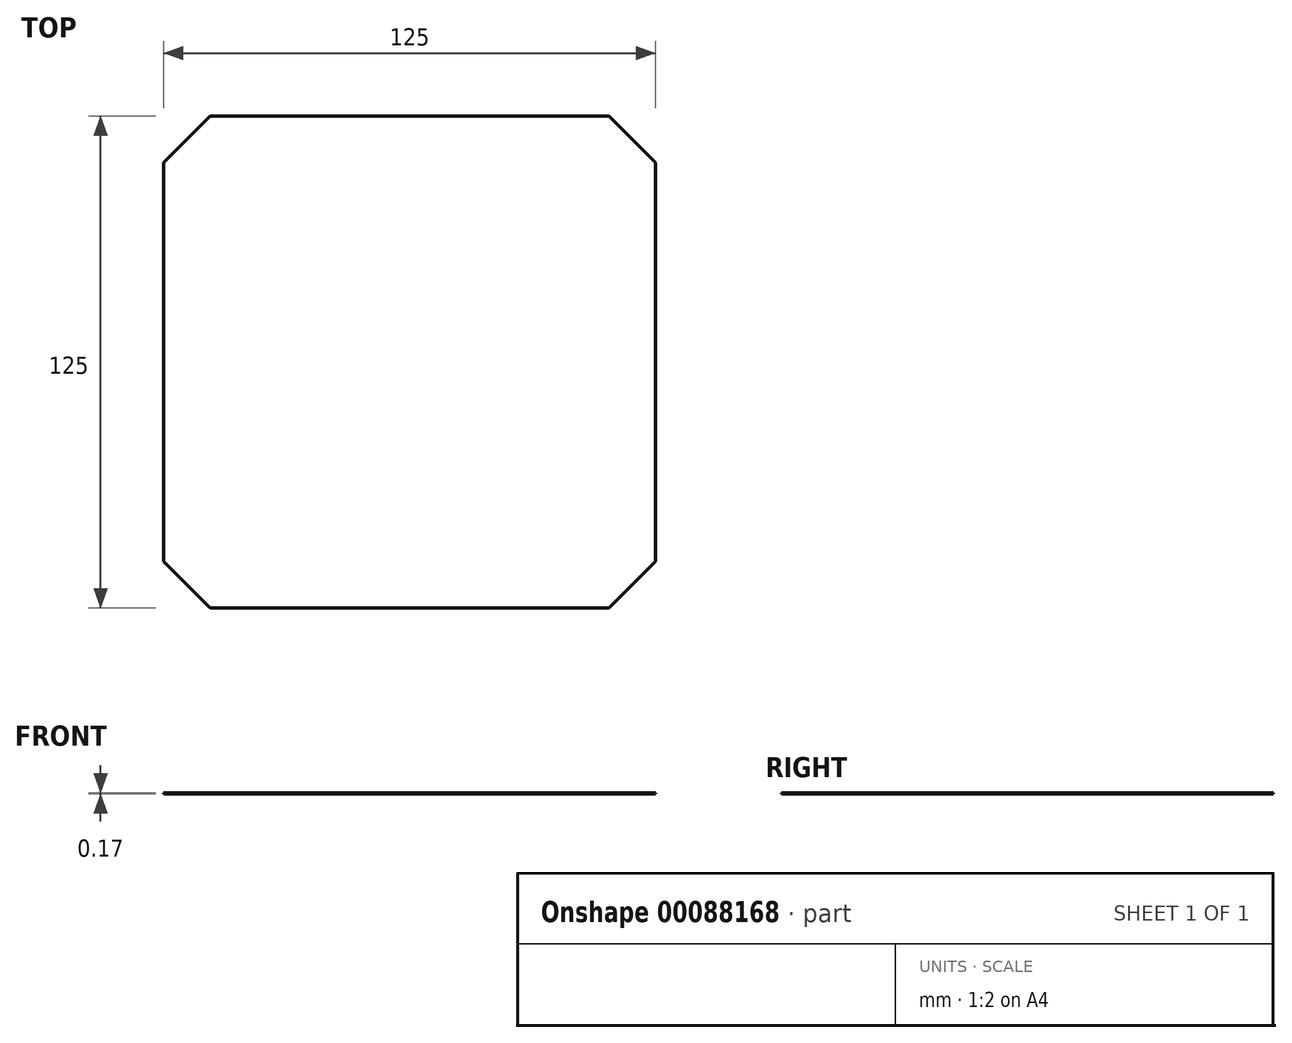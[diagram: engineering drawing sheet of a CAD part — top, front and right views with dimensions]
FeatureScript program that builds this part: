
annotation { "Feature Type Name" : "Feature", "Feature Type Description" : "" }
export const myFeature = defineFeature(function(context is Context, id is Id, definition is map)
    precondition{}
    {
        {
            var Q0;
            Q0=qCreatedBy(makeId("Top.planeOp"),FACE);
            var sketch = newSketch(context, id + "F0", { "sketchPlane" : qUnion([Q0])});
            skLineSegment(sketch, "E0.bottom", {"start": v(-50.64, 62.5) * mm, "end": v(50.64, 62.5) * mm});
            skLineSegment(sketch, "E0.top", {"start": v(-50.64, -62.5) * mm, "end": v(50.64, -62.5) * mm});
            skLineSegment(sketch, "E0.left", {"start": v(-62.5, 50.64) * mm, "end": v(-62.5, -50.64) * mm});
            skLineSegment(sketch, "E0.right", {"start": v(62.5, 50.64) * mm, "end": v(62.5, -50.64) * mm});
            skLineSegment(sketch, "E1", {"start": v(62.5, -50.64) * mm, "end": v(50.64, -62.5) * mm});
            skLineSegment(sketch, "E2", {"start": v(-50.64, -62.5) * mm, "end": v(-62.5, -50.64) * mm});
            skLineSegment(sketch, "E3", {"start": v(62.5, 50.64) * mm, "end": v(50.64, 62.5) * mm});
            skLineSegment(sketch, "E4", {"start": v(-50.64, 62.5) * mm, "end": v(-62.5, 50.64) * mm});
            skSolve(sketch);
        }
        {
            var Q0;
            Q0 = qSketchRegion(id + "F0", true);
            extrude(context, id + "F1", {"entities" : qUnion([Q0]), "depth" : 0.17 * mm});
        }
    });
